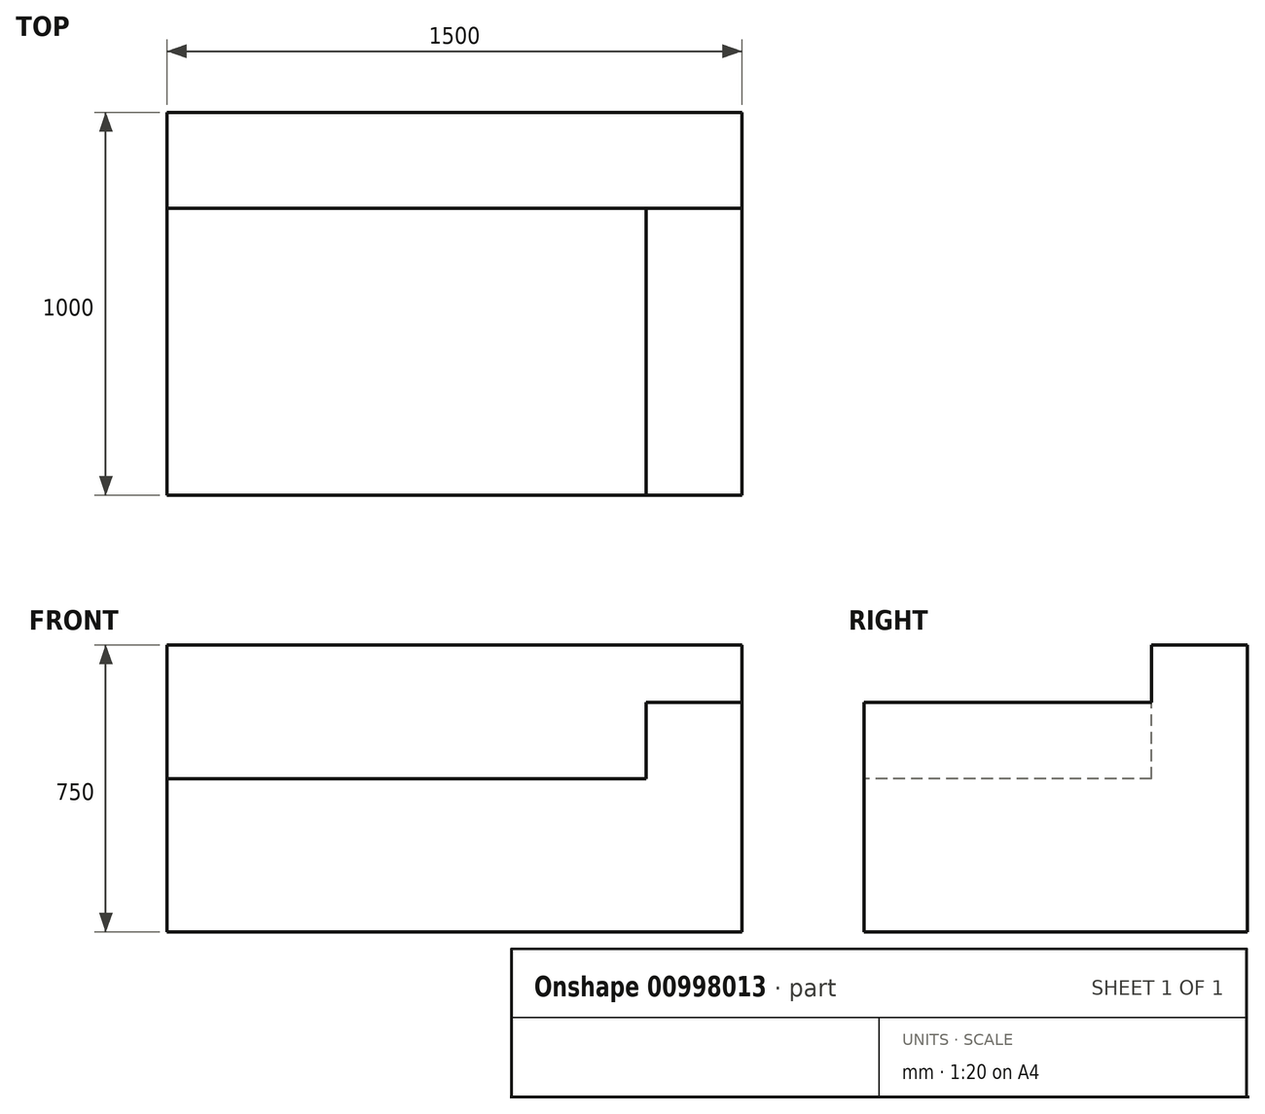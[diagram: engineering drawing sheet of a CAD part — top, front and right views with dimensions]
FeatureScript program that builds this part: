
annotation { "Feature Type Name" : "Feature", "Feature Type Description" : "" }
export const myFeature = defineFeature(function(context is Context, id is Id, definition is map)
    precondition{}
    {
        {
            var Q0;
            Q0=qCreatedBy(makeId("Top.planeOp"),FACE);
            var sketch = newSketch(context, id + "F0", { "sketchPlane" : qUnion([Q0])});
            skLineSegment(sketch, "E0", {"start": v(0, 0) * mm, "end": v(0, 1254.28) * mm, "construction": true});
            skLineSegment(sketch, "E1", {"start": v(0, 0) * mm, "end": v(-1220.88, 0) * mm, "construction": true});
            skLineSegment(sketch, "E2.bottom", {"start": v(-750, 500) * mm, "end": v(750, 500) * mm});
            skLineSegment(sketch, "E2.top", {"start": v(-750, -500) * mm, "end": v(750, -500) * mm});
            skLineSegment(sketch, "E2.left", {"start": v(-750, 500) * mm, "end": v(-750, -500) * mm});
            skLineSegment(sketch, "E2.right", {"start": v(750, 500) * mm, "end": v(750, -500) * mm});
            skSolve(sketch);
        }
        {
            var Q0;
            Q0 = qSketchRegion(id + "F0", true);
            extrude(context, id + "F1", {"entities" : qUnion([Q0]), "depth" : 750 * mm, "offsetDistance" : 25 * mm});
        }
        {
            var Q0;
            Q0=makeQuery(id+"F1.opExtrude","CAP_FACE",FACE,{"disambiguationData":[OSD([sQuery(id+"F0.wireOp",EDGE,"E2.bottom"),sQuery(id+"F0.wireOp",EDGE,"E2.top"),sQuery(id+"F0.wireOp",EDGE,"E2.left"),sQuery(id+"F0.wireOp",EDGE,"E2.right")])],"isStart":false});
            var sketch = newSketch(context, id + "F2", { "sketchPlane" : qUnion([Q0])});
            skLineSegment(sketch, "E3.bottom", {"start": v(-750, 250) * mm, "end": v(500, 250) * mm});
            skLineSegment(sketch, "E3.top", {"start": v(-750, -500) * mm, "end": v(500, -500) * mm});
            skLineSegment(sketch, "E3.left", {"start": v(-750, 250) * mm, "end": v(-750, -500) * mm});
            skLineSegment(sketch, "E3.right", {"start": v(500, 250) * mm, "end": v(500, -500) * mm});
            skSolve(sketch);
        }
        {
            var Q0;
            Q0 = qSketchRegion(id + "F2", true);
            extrude(context, id + "F3", {"entities" : qUnion([Q0]), "operationType" : NewBodyOperationType.REMOVE, "oppositeDirection" : true, "depth" : 350 * mm, "offsetDistance" : 25 * mm});
        }
        {
            var Q0;
            Q0=makeQuery(id+"F1.opExtrude","CAP_FACE",FACE,{"disambiguationData":[OSD([sQuery(id+"F0.wireOp",EDGE,"E2.bottom"),sQuery(id+"F0.wireOp",EDGE,"E2.top"),sQuery(id+"F0.wireOp",EDGE,"E2.left"),sQuery(id+"F0.wireOp",EDGE,"E2.right")])],"isStart":false});
            var sketch = newSketch(context, id + "F4", { "sketchPlane" : qUnion([Q0])});
            skLineSegment(sketch, "E4", {"start": v(500, 250) * mm, "end": v(750, 250) * mm});
            skSolve(sketch);
        }
        {
            var Q0;
            Q0 = qSketchRegion(id + "F4", true);
            var Q1;
            {var subQ0=sQuery(id+"F4.wireOp",EDGE,"E4");Q1=makeQuery(id+"F4.imprint","IMPRINT",FACE,{"disambiguationData":[TD([[makeQuery(id+"F4.imprint","IMPRINT",EDGE,{"derivedFrom":subQ0}),-1.0]])]});}
            extrude(context, id + "F5", {"entities" : qUnion([Q0, Q1]), "operationType" : NewBodyOperationType.REMOVE, "oppositeDirection" : true, "depth" : 150 * mm, "offsetDistance" : 25 * mm});
        }
    });
